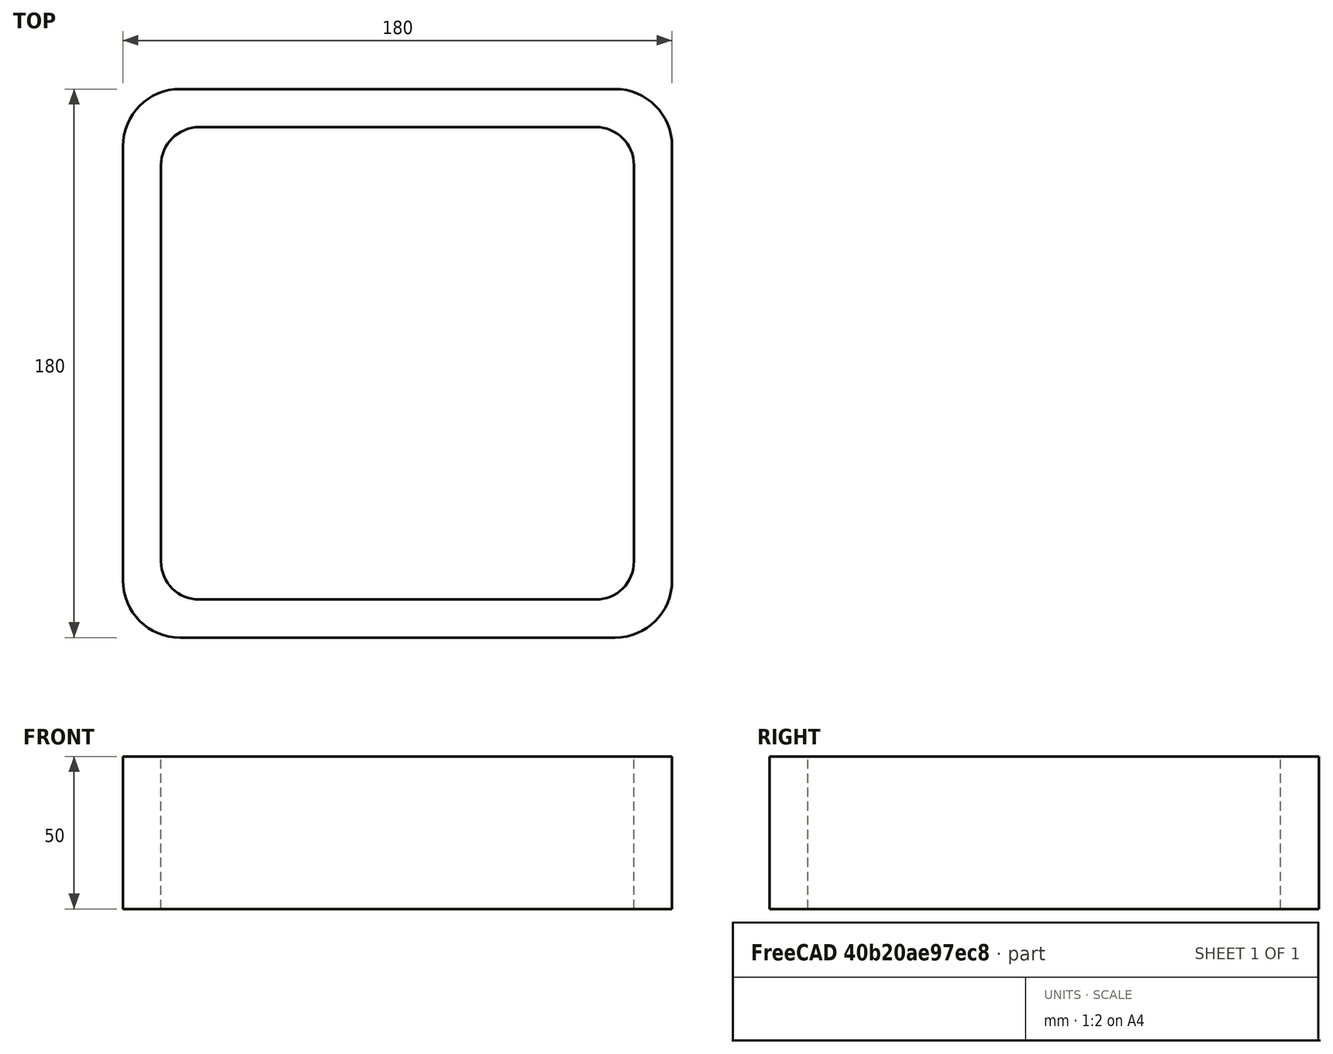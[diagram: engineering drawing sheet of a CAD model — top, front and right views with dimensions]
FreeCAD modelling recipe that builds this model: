
FCSTD DOCUMENT  (FreeCAD 0.15R4671 (Git))
Label: Square hollow section 180x180x12.5 EN10219 S235JRH
License: All rights reserved
LicenseURL: http://en.wikipedia.org/wiki/All_rights_reserved
objects: Sketcher::SketchObject×1, Part::Extrusion×1
note: 2 computed .brp shape members not serialized (recipe doc carries the construction recipe); baked Part::Feature solids carry a one-line shape summary decoded from their .brp

FEATURE [Sketcher::SketchObject] Sketch
  sketch-geometry (16):
    g0: LineSegment StartX=-65 StartY=77.5 StartZ=0 EndX=65 EndY=77.5 EndZ=0
    g1: LineSegment StartX=77.5 StartY=65 StartZ=0 EndX=77.5 EndY=-65 EndZ=0
    g2: LineSegment StartX=65 StartY=-77.5 StartZ=0 EndX=-65 EndY=-77.5 EndZ=0
    g3: LineSegment StartX=-77.5 StartY=-65 StartZ=0 EndX=-77.5 EndY=65 EndZ=0
    g4: LineSegment StartX=-71.25 StartY=90 StartZ=0 EndX=71.25 EndY=90 EndZ=0
    g5: LineSegment StartX=90 StartY=71.25 StartZ=0 EndX=90 EndY=-71.25 EndZ=0
    g6: LineSegment StartX=71.25 StartY=-90 StartZ=0 EndX=-71.25 EndY=-90 EndZ=0
    g7: LineSegment StartX=-90 StartY=-71.25 StartZ=0 EndX=-90 EndY=71.25 EndZ=0
    g8: ArcOfCircle CenterX=-65 CenterY=65 CenterZ=0 NormalX=0 NormalY=0 NormalZ=1 Radius=12.5 StartAngle=1.5708 EndAngle=3.14159
    g9: ArcOfCircle CenterX=65 CenterY=65 CenterZ=0 NormalX=0 NormalY=0 NormalZ=1 Radius=12.5 StartAngle=0 EndAngle=1.5708
    g10: ArcOfCircle CenterX=65 CenterY=-65 CenterZ=0 NormalX=0 NormalY=0 NormalZ=1 Radius=12.5 StartAngle=4.71239 EndAngle=6.28319
    g11: ArcOfCircle CenterX=-65 CenterY=-65 CenterZ=0 NormalX=0 NormalY=0 NormalZ=1 Radius=12.5 StartAngle=3.14159 EndAngle=4.71239
    g12: ArcOfCircle CenterX=71.25 CenterY=71.25 CenterZ=0 NormalX=0 NormalY=0 NormalZ=1 Radius=18.75 StartAngle=0 EndAngle=1.5708
    g13: ArcOfCircle CenterX=71.25 CenterY=-71.25 CenterZ=0 NormalX=0 NormalY=0 NormalZ=1 Radius=18.75 StartAngle=4.71239 EndAngle=6.28319
    g14: ArcOfCircle CenterX=-71.25 CenterY=-71.25 CenterZ=0 NormalX=0 NormalY=0 NormalZ=1 Radius=18.75 StartAngle=3.14159 EndAngle=4.71239
    g15: ArcOfCircle CenterX=-71.25 CenterY=71.25 CenterZ=0 NormalX=0 NormalY=0 NormalZ=1 Radius=18.75 StartAngle=1.5708 EndAngle=3.14159
  constraints (36):
    c: Horizontal(g2)
    c: Vertical(g3)
    c: Horizontal(g6)
    c: Vertical(g7)
    c: Tangent(g3,g8) = 1.5708
    c: Tangent(g0,g8) = 1.5708
    c: Tangent(g0,g9) = 1.5708
    c: Tangent(g1,g9) = 1.5708
    c: Tangent(g1,g10) = 1.5708
    c: Tangent(g2,g10) = 1.5708
    c: Tangent(g2,g11) = 1.5708
    c: Tangent(g3,g11) = 1.5708
    c: Tangent(g4,g12) = 1.5708
    c: Tangent(g5,g12) = 1.5708
    c: Tangent(g5,g13) = 1.5708
    c: Tangent(g6,g13) = 1.5708
    c: Tangent(g6,g14) = 1.5708
    c: Tangent(g7,g14) = 1.5708
    c: Tangent(g7,g15) = 1.5708
    c: Tangent(g4,g15) = 1.5708
    c: Equal(g9,g8)
    c: Equal(g9,g11)
    c: Equal(g9,g10)
    c: Equal(g12,g15)
    c: Equal(g12,g14)
    c: Equal(g12,g13)
    c: Symmetric(g4,g6,g-1)
    c: Symmetric(g7,g5,g-2)
    c: DistanceY(g4,g6) = -180
    c: DistanceX(g7,g5) = 180
    c: Symmetric(g3,g1,g-2)
    c: Symmetric(g0,g2,g-1)
    c: DistanceY(g0,g4) = 12.5
    c: DistanceX(g5,g1) = -12.5
    c: Radius(g9) = 12.5
    c: Radius(g12) = 18.75
FEATURE [Part::Extrusion] Extrude  label="Square hollow section 180x180x12.5 EN10219 S235JRH"
  Base = -> Sketch
  Dir = (0,0,50)
  Solid = true
